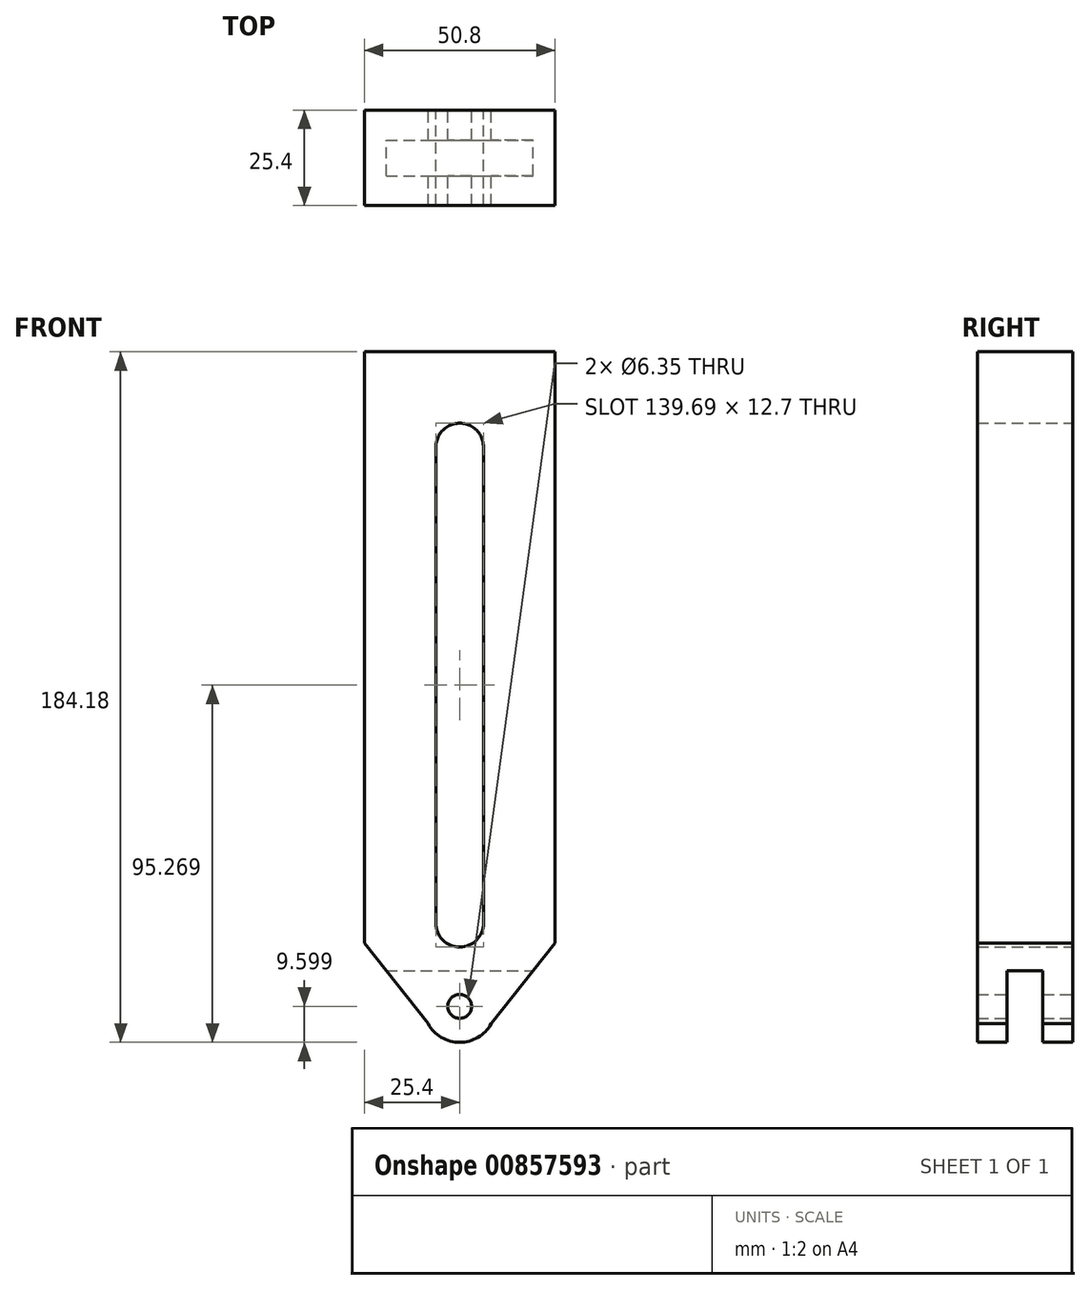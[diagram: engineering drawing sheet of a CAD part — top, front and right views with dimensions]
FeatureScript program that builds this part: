
annotation { "Feature Type Name" : "Feature", "Feature Type Description" : "" }
export const myFeature = defineFeature(function(context is Context, id is Id, definition is map)
    precondition{}
    {
        {
            var Q0;
            Q0=qCreatedBy(makeId("Front.planeOp"),FACE);
            var sketch = newSketch(context, id + "F0", { "sketchPlane" : qUnion([Q0])});
            skLineSegment(sketch, "E0.top", {"start": v(25.4, 92.08) * mm, "end": v(-25.4, 92.08) * mm});
            skLineSegment(sketch, "E0.left", {"start": v(25.4, -65.67) * mm, "end": v(25.4, 92.08) * mm});
            skLineSegment(sketch, "E0.right", {"start": v(-25.4, -65.67) * mm, "end": v(-25.4, 92.08) * mm});
            skPoint(sketch, "E0.middle", {"position": v(0, 0) * mm});
            skPoint(sketch, "E1", {"position": v(0, -82.55) * mm});
            skPoint(sketch, "E2", {"position": v(9.53, -82.55) * mm});
            skPoint(sketch, "E3", {"position": v(-9.52, -82.55) * mm});
            skPoint(sketch, "E4", {"position": v(9.52, -69.85) * mm});
            skPoint(sketch, "E5", {"position": v(-9.53, -66.66) * mm});
            skArc(sketch, "E6", {"start": v(-9.52, -82.55) * mm, "mid": v(0, -92.19) * mm, "end": v(9.52, -82.55) * mm, "construction": true});
            skLineSegment(sketch, "E7", {"start": v(-25.4, -65.67) * mm, "end": v(-8.41, -87.13) * mm, "construction": true});
            skLineSegment(sketch, "E8", {"start": v(-8.41, -87.13) * mm, "end": v(8.41, -87.13) * mm, "construction": true});
            skLineSegment(sketch, "E9", {"start": v(8.41, -87.13) * mm, "end": v(25.4, -65.67) * mm, "construction": true});
            skLineSegment(sketch, "E10", {"start": v(25.4, -65.67) * mm, "end": v(8.41, -87.13) * mm});
            skLineSegment(sketch, "E11", {"start": v(-25.4, -65.67) * mm, "end": v(-8.41, -87.13) * mm});
            skArc(sketch, "E12", {"start": v(-8.41, -87.13) * mm, "mid": v(0, -92.1) * mm, "end": v(8.41, -87.13) * mm});
            skPoint(sketch, "E13.orphan", {"position": v(-25.4, -92.08) * mm});
            skPoint(sketch, "E14.orphan", {"position": v(25.4, -92.07) * mm});
            skPoint(sketch, "E15", {"position": v(0, -66.68) * mm});
            skPoint(sketch, "E16", {"position": v(0, -60.33) * mm});
            skPoint(sketch, "E17", {"position": v(0, 66.68) * mm});
            skCircle(sketch, "E18", {"center": v(0, 66.68) * mm, "radius": 6.35 * mm, "construction": true});
            skCircle(sketch, "E19", {"center": v(0, -60.33) * mm, "radius": 6.35 * mm, "construction": true});
            skLineSegment(sketch, "E20", {"start": v(-6.21, 68) * mm, "end": v(-6.21, -61.65) * mm, "construction": true});
            skLineSegment(sketch, "E21", {"start": v(6.35, 66.62) * mm, "end": v(6.35, -60.32) * mm, "construction": true});
            skPoint(sketch, "E22", {"position": v(-6.35, 66.66) * mm});
            skPoint(sketch, "E23", {"position": v(-6.35, -60.33) * mm});
            skLineSegment(sketch, "E24", {"start": v(-6.35, -60.33) * mm, "end": v(-6.35, 66.66) * mm, "construction": true});
            skLineSegment(sketch, "E25", {"start": v(-6.35, 66.66) * mm, "end": v(-6.35, -60.33) * mm});
            skLineSegment(sketch, "E26", {"start": v(6.35, -60.32) * mm, "end": v(6.35, 66.62) * mm});
            skArc(sketch, "E27", {"start": v(6.35, 66.62) * mm, "mid": v(0.02, 73.01) * mm, "end": v(-6.35, 66.66) * mm});
            skArc(sketch, "E28", {"start": v(-6.35, -60.33) * mm, "mid": v(0, -66.67) * mm, "end": v(6.35, -60.32) * mm});
            skCircle(sketch, "E29", {"center": v(0, -82.5) * mm, "radius": 3.18 * mm});
            skSolve(sketch);
        }
        {
            var Q0;
            Q0=makeQuery(id+"F0.imprint","IMPRINT",FACE,{"disambiguationData":[TD([[makeQuery(id+"F0.imprint","IMPRINT",EDGE,{"derivedFrom":sQuery(id+"F0.wireOp",EDGE,"E0.top")}),1.0]])]});
            extrude(context, id + "F1", {"entities" : qUnion([Q0]), "depth" : 25.4 * mm, "offsetDistance" : 25.4 * mm});
        }
        {
            var Q0;
            Q0=makeQuery(id+"F1.opExtrude","SWEPT_FACE",FACE,{"disambiguationData":[OSD([sQuery(id+"F0.wireOp",EDGE,"E0.left")])]});
            var sketch = newSketch(context, id + "F2", { "sketchPlane" : qUnion([Q0])});
            skPoint(sketch, "E30", {"position": v(-12.7, -73.03) * mm});
            skPoint(sketch, "E30.positionSnap0", {"position": v(-12.7, -65.67) * mm});
            skPoint(sketch, "E31", {"position": v(-17.46, -73.03) * mm});
            skPoint(sketch, "E32", {"position": v(-7.94, -73.03) * mm});
            skLineSegment(sketch, "E33.bottom", {"start": v(-17.46, -73.03) * mm, "end": v(-7.94, -73.03) * mm});
            skLineSegment(sketch, "E33.top", {"start": v(-17.46, -105) * mm, "end": v(-7.94, -105) * mm});
            skLineSegment(sketch, "E33.left", {"start": v(-17.46, -73.03) * mm, "end": v(-17.46, -105) * mm});
            skLineSegment(sketch, "E33.right", {"start": v(-7.94, -73.03) * mm, "end": v(-7.94, -105) * mm});
            skSolve(sketch);
        }
        {
            var Q0;
            Q0=makeQuery(id+"F2.imprint","IMPRINT",FACE,{"disambiguationData":[TD([[makeQuery(id+"F2.imprint","IMPRINT",EDGE,{"derivedFrom":sQuery(id+"F2.wireOp",EDGE,"E33.bottom")}),-1.0]])]});
            extrude(context, id + "F3", {"entities" : qUnion([Q0]), "operationType" : NewBodyOperationType.REMOVE, "endBound" : BoundingType.THROUGH_ALL, "oppositeDirection" : true, "depth" : 25.4 * mm, "offsetDistance" : 25.4 * mm});
        }
    });
